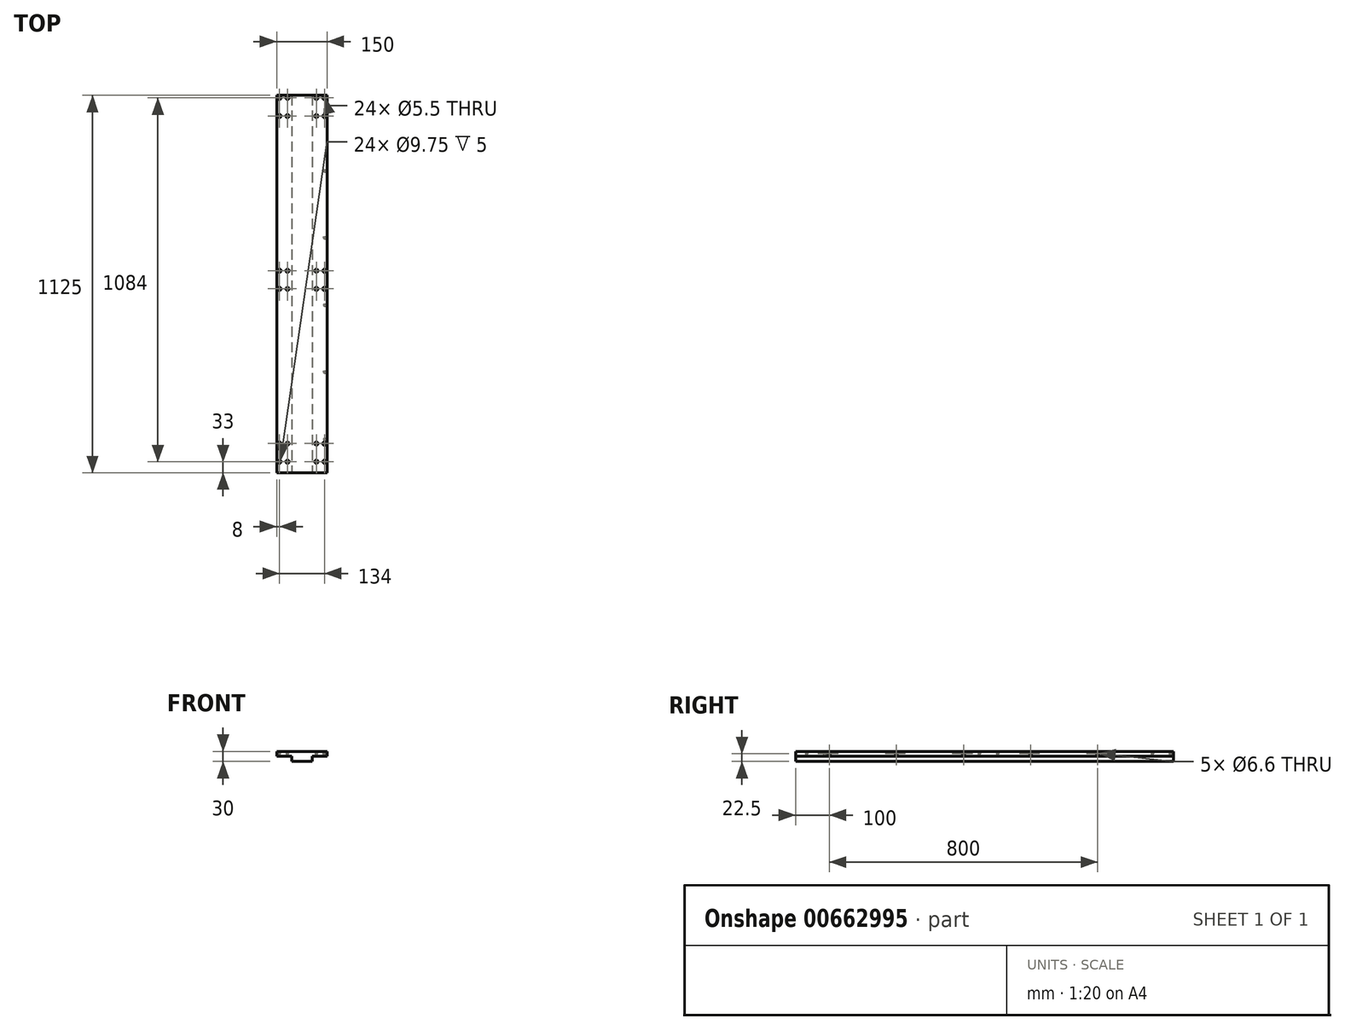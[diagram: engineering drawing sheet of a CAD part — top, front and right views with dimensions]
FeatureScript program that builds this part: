
annotation { "Feature Type Name" : "Feature", "Feature Type Description" : "" }
export const myFeature = defineFeature(function(context is Context, id is Id, definition is map)
    precondition{}
    {
        {
            var Q0;
            Q0=qCreatedBy(makeId("Front.planeOp"),FACE);
            var sketch = newSketch(context, id + "F0", { "sketchPlane" : qUnion([Q0])});
            skLineSegment(sketch, "E0.bottom", {"start": v(75, -15) * mm, "end": v(-75, -15) * mm});
            skLineSegment(sketch, "E0.top", {"start": v(75, 15) * mm, "end": v(-75, 15) * mm});
            skLineSegment(sketch, "E0.left", {"start": v(75, -15) * mm, "end": v(75, 15) * mm});
            skLineSegment(sketch, "E0.right", {"start": v(-75, -15) * mm, "end": v(-75, 15) * mm});
            skPoint(sketch, "E0.middle", {"position": v(0, 0) * mm});
            skSolve(sketch);
        }
        {
            var Q0;
            Q0=makeQuery(id+"F0.imprint","IMPRINT",FACE,{"disambiguationData":[TD([[makeQuery(id+"F0.imprint","IMPRINT",EDGE,{"derivedFrom":sQuery(id+"F0.wireOp",EDGE,"E0.bottom")}),-1.0]])]});
            extrude(context, id + "F1", {"entities" : qUnion([Q0]), "depth" : 1125 * mm, "offsetDistance" : 25 * mm});
        }
        {
            var Q0;
            Q0=makeQuery(id+"F1.opExtrude","SWEPT_FACE",FACE,{"disambiguationData":[OSD([sQuery(id+"F0.wireOp",EDGE,"E0.top")])]});
            var sketch = newSketch(context, id + "F2", { "sketchPlane" : qUnion([Q0])});
            skLineSegment(sketch, "E1.bottom", {"start": v(-67, -1092) * mm, "end": v(-43, -1092) * mm, "construction": true});
            skLineSegment(sketch, "E1.top", {"start": v(-67, -1038) * mm, "end": v(-43, -1038) * mm, "construction": true});
            skLineSegment(sketch, "E1.left", {"start": v(-67, -1092) * mm, "end": v(-67, -1038) * mm, "construction": true});
            skLineSegment(sketch, "E1.right", {"start": v(-43, -1092) * mm, "end": v(-43, -1038) * mm, "construction": true});
            skLineSegment(sketch, "E2.bottom", {"start": v(43, -1092) * mm, "end": v(67, -1092) * mm, "construction": true});
            skLineSegment(sketch, "E2.top", {"start": v(43, -1038) * mm, "end": v(67, -1038) * mm, "construction": true});
            skLineSegment(sketch, "E2.left", {"start": v(43, -1092) * mm, "end": v(43, -1038) * mm, "construction": true});
            skLineSegment(sketch, "E2.right", {"start": v(67, -1092) * mm, "end": v(67, -1038) * mm, "construction": true});
            skLineSegment(sketch, "E3.bottom", {"start": v(-67, -8) * mm, "end": v(-43, -8) * mm, "construction": true});
            skLineSegment(sketch, "E3.top", {"start": v(-67, -62) * mm, "end": v(-43, -62) * mm, "construction": true});
            skLineSegment(sketch, "E3.left", {"start": v(-67, -8) * mm, "end": v(-67, -62) * mm, "construction": true});
            skLineSegment(sketch, "E3.right", {"start": v(-43, -8) * mm, "end": v(-43, -62) * mm, "construction": true});
            skLineSegment(sketch, "E4.bottom", {"start": v(43, -8) * mm, "end": v(67, -8) * mm, "construction": true});
            skLineSegment(sketch, "E4.top", {"start": v(43, -62) * mm, "end": v(67, -62) * mm, "construction": true});
            skLineSegment(sketch, "E4.left", {"start": v(43, -8) * mm, "end": v(43, -62) * mm, "construction": true});
            skLineSegment(sketch, "E4.right", {"start": v(67, -8) * mm, "end": v(67, -62) * mm, "construction": true});
            skLineSegment(sketch, "E5.bottom", {"start": v(-67, -523) * mm, "end": v(-43, -523) * mm, "construction": true});
            skLineSegment(sketch, "E5.top", {"start": v(-67, -577) * mm, "end": v(-43, -577) * mm, "construction": true});
            skLineSegment(sketch, "E5.left", {"start": v(-67, -523) * mm, "end": v(-67, -577) * mm, "construction": true});
            skLineSegment(sketch, "E5.right", {"start": v(-43, -523) * mm, "end": v(-43, -577) * mm, "construction": true});
            skLineSegment(sketch, "E6.bottom", {"start": v(43, -523) * mm, "end": v(67, -523) * mm, "construction": true});
            skLineSegment(sketch, "E6.top", {"start": v(43, -577) * mm, "end": v(67, -577) * mm, "construction": true});
            skLineSegment(sketch, "E6.left", {"start": v(43, -523) * mm, "end": v(43, -577) * mm, "construction": true});
            skLineSegment(sketch, "E6.right", {"start": v(67, -523) * mm, "end": v(67, -577) * mm, "construction": true});
            skLineSegment(sketch, "E7", {"start": v(-43, -1092) * mm, "end": v(43, -1092) * mm, "construction": true});
            skLineSegment(sketch, "E8", {"start": v(-67, -1038) * mm, "end": v(-67, -577) * mm, "construction": true});
            skLineSegment(sketch, "E9", {"start": v(67, -577) * mm, "end": v(67, -1038) * mm, "construction": true});
            skLineSegment(sketch, "E10", {"start": v(-67, -523) * mm, "end": v(-67, -62) * mm, "construction": true});
            skLineSegment(sketch, "E11", {"start": v(67, -62) * mm, "end": v(67, -523) * mm, "construction": true});
            skLineSegment(sketch, "E12", {"start": v(-43, -8) * mm, "end": v(43, -8) * mm, "construction": true});
            skSolve(sketch);
        }
        {
            var Q0;
            Q0=sQuery(id+"F2.wireOp",VERTEX,"E1.bottom.start");
            var Q1;
            Q1=sQuery(id+"F2.wireOp",VERTEX,"E1.top.start");
            var Q2;
            Q2=sQuery(id+"F2.wireOp",VERTEX,"E1.top.end");
            var Q3;
            Q3=sQuery(id+"F2.wireOp",VERTEX,"E1.bottom.end");
            var Q4;
            Q4=sQuery(id+"F2.wireOp",VERTEX,"E2.bottom.start");
            var Q5;
            Q5=sQuery(id+"F2.wireOp",VERTEX,"E2.bottom.end");
            var Q6;
            Q6=sQuery(id+"F2.wireOp",VERTEX,"E2.top.end");
            var Q7;
            Q7=sQuery(id+"F2.wireOp",VERTEX,"E2.top.start");
            var Q8;
            Q8=sQuery(id+"F2.wireOp",VERTEX,"E5.top.start");
            var Q9;
            Q9=sQuery(id+"F2.wireOp",VERTEX,"E5.top.end");
            var Q10;
            Q10=sQuery(id+"F2.wireOp",VERTEX,"E5.bottom.end");
            var Q11;
            Q11=sQuery(id+"F2.wireOp",VERTEX,"E5.bottom.start");
            var Q12;
            Q12=sQuery(id+"F2.wireOp",VERTEX,"E6.bottom.start");
            var Q13;
            Q13=sQuery(id+"F2.wireOp",VERTEX,"E6.bottom.end");
            var Q14;
            Q14=sQuery(id+"F2.wireOp",VERTEX,"E6.top.end");
            var Q15;
            Q15=sQuery(id+"F2.wireOp",VERTEX,"E6.top.start");
            var Q16;
            Q16=sQuery(id+"F2.wireOp",VERTEX,"E4.top.start");
            var Q17;
            Q17=sQuery(id+"F2.wireOp",VERTEX,"E4.bottom.start");
            var Q18;
            Q18=sQuery(id+"F2.wireOp",VERTEX,"E4.bottom.end");
            var Q19;
            Q19=sQuery(id+"F2.wireOp",VERTEX,"E4.top.end");
            var Q20;
            Q20=sQuery(id+"F2.wireOp",VERTEX,"E3.top.end");
            var Q21;
            Q21=sQuery(id+"F2.wireOp",VERTEX,"E3.top.start");
            var Q22;
            Q22=sQuery(id+"F2.wireOp",VERTEX,"E3.bottom.start");
            var Q23;
            Q23=sQuery(id+"F2.wireOp",VERTEX,"E3.bottom.end");
            var Q24;
            Q24=makeQuery(id+"F1.opExtrude","SWEPT_BODY",BODY,{"disambiguationData":[OSD([sQuery(id+"F0.wireOp",EDGE,"E0.bottom"),sQuery(id+"F0.wireOp",EDGE,"E0.top"),sQuery(id+"F0.wireOp",EDGE,"E0.left"),sQuery(id+"F0.wireOp",EDGE,"E0.right")])]});
            hole(context, id + "F3", {"style" : HoleStyle.C_BORE, "endStyle" : HoleEndStyle.THROUGH, "standardTappedOrClearance" : lookupTablePath({ "fit" : "Normal", "standard" : "ISO", "size" : "M5", "type" : "Clearance" }), "standardBlindInLast" : lookupTablePath({ "fit" : "Normal", "standard" : "ISO", "engagement" : "75%", "pitch" : "0.8 mm", "size" : "M5", "type" : "Clearance & tapped" }), "holeDiameter" : 5.5 * mm, "cBoreDiameter" : 9.75 * mm, "cBoreDepth" : 5 * mm, "majorDiameter" : 5 * mm, "isTappedThrough" : true, "tappedDepth" : 12 * mm, "tapClearance" : 3, "locations" : qUnion([Q0, Q1, Q2, Q3, Q4, Q5, Q6, Q7, Q8, Q9, Q10, Q11, Q12, Q13, Q14, Q15, Q16, Q17, Q18, Q19, Q20, Q21, Q22, Q23]), "scope" : qUnion([Q24])});
        }
        {
            var Q0;
            Q0=makeQuery(id+"F1.opExtrude","CAP_FACE",FACE,{"disambiguationData":[OSD([sQuery(id+"F0.wireOp",EDGE,"E0.bottom"),sQuery(id+"F0.wireOp",EDGE,"E0.top"),sQuery(id+"F0.wireOp",EDGE,"E0.left"),sQuery(id+"F0.wireOp",EDGE,"E0.right")])],"isStart":false});
            var sketch = newSketch(context, id + "F4", { "sketchPlane" : qUnion([Q0])});
            skLineSegment(sketch, "E13", {"start": v(-75, 0) * mm, "end": v(-30, 0) * mm});
            skLineSegment(sketch, "E14", {"start": v(-30, 0) * mm, "end": v(-30, -15) * mm});
            skLineSegment(sketch, "E15", {"start": v(75, 0) * mm, "end": v(30, 0) * mm});
            skLineSegment(sketch, "E16", {"start": v(30, 0) * mm, "end": v(30, -15) * mm});
            skSolve(sketch);
        }
        {
            var Q0;
            {var subQ0=sQuery(id+"F4.wireOp",EDGE,"E13");Q0=makeQuery(id+"F4.imprint","IMPRINT",FACE,{"disambiguationData":[TD([[makeQuery(id+"F4.imprint","IMPRINT",EDGE,{"derivedFrom":subQ0}),-1.0]])]});}
            var Q1;
            {var subQ0=sQuery(id+"F4.wireOp",EDGE,"E15");Q1=makeQuery(id+"F4.imprint","IMPRINT",FACE,{"disambiguationData":[TD([[makeQuery(id+"F4.imprint","IMPRINT",EDGE,{"derivedFrom":subQ0}),1.0]])]});}
            extrude(context, id + "F5", {"entities" : qUnion([Q0, Q1]), "operationType" : NewBodyOperationType.REMOVE, "endBound" : BoundingType.THROUGH_ALL, "oppositeDirection" : true, "depth" : 25 * mm, "offsetDistance" : 25 * mm});
        }
        {
            var Q0;
            Q0=makeQuery(id+"F1.opExtrude","SWEPT_FACE",FACE,{"disambiguationData":[OSD([sQuery(id+"F0.wireOp",EDGE,"E0.left")])]});
            var sketch = newSketch(context, id + "F6", { "sketchPlane" : qUnion([Q0])});
            skPoint(sketch, "E17", {"position": v(-1025, 7.5) * mm});
            skPoint(sketch, "E18", {"position": v(-825, 7.5) * mm});
            skPoint(sketch, "E19", {"position": v(-625, 7.5) * mm});
            skPoint(sketch, "E20", {"position": v(-425, 7.5) * mm});
            skLineSegment(sketch, "E21", {"start": v(-1025, 7.5) * mm, "end": v(-825, 7.5) * mm, "construction": true});
            skLineSegment(sketch, "E22", {"start": v(-825, 7.5) * mm, "end": v(-625, 7.5) * mm, "construction": true});
            skLineSegment(sketch, "E23", {"start": v(-425, 7.5) * mm, "end": v(-625, 7.5) * mm, "construction": true});
            skPoint(sketch, "E24", {"position": v(-225, 7.5) * mm});
            skLineSegment(sketch, "E25", {"start": v(-425, 7.5) * mm, "end": v(-225, 7.5) * mm, "construction": true});
            skSolve(sketch);
        }
        {
            var Q0;
            Q0=sQuery(id+"F6.wireOp",VERTEX,"E17");
            var Q1;
            Q1=sQuery(id+"F6.wireOp",VERTEX,"E18");
            var Q2;
            Q2=sQuery(id+"F6.wireOp",VERTEX,"E19");
            var Q3;
            Q3=sQuery(id+"F6.wireOp",VERTEX,"E20");
            var Q4;
            Q4=sQuery(id+"F6.wireOp",VERTEX,"E24");
            var Q5;
            Q5=makeQuery(id+"F1.opExtrude","SWEPT_BODY",BODY,{"disambiguationData":[OSD([sQuery(id+"F0.wireOp",EDGE,"E0.bottom"),sQuery(id+"F0.wireOp",EDGE,"E0.top"),sQuery(id+"F0.wireOp",EDGE,"E0.left"),sQuery(id+"F0.wireOp",EDGE,"E0.right")])]});
            hole(context, id + "F7", {"style" : HoleStyle.SIMPLE, "endStyle" : HoleEndStyle.BLIND, "standardTappedOrClearance" : lookupTablePath({ "fit" : "Normal", "standard" : "ISO", "size" : "M6", "type" : "Clearance" }), "standardBlindInLast" : lookupTablePath({ "fit" : "Normal", "standard" : "ISO", "engagement" : "75%", "pitch" : "1 mm", "size" : "M6", "type" : "Clearance & tapped" }), "holeDiameter" : 6.6 * mm, "majorDiameter" : 5 * mm, "holeDepth" : 9 * mm, "isTappedThrough" : true, "tappedDepth" : 12 * mm, "tapClearance" : 3, "locations" : qUnion([Q0, Q1, Q2, Q3, Q4]), "scope" : qUnion([Q5])});
        }
    });
